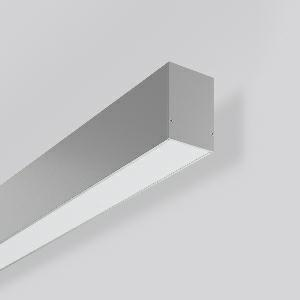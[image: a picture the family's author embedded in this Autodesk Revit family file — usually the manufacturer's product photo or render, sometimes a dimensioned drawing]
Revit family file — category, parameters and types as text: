
# Revit family: less_is_more_50_312607_0045_1_136a
name_source: partatom
category: Lighting Fixtures
units: mm (PartAtom-declared; Revit-internal decimal feet)

## family parameters
Cut with Voids When Loaded = No
Host = Face
Light Source = No
Part Type = Normal
Room Calculation Point = No
Round Connector Dimension = Use Diameter
Shared = No

## types (1)
- LESS IS MORE 50 (1 x LED Modul 840, 1500 lm, 4000)
    Apparent Load = 12 VA
    CIE Flux Codes = 48 80 96 100 100
    Color Rendering = 80
    Color Temperature = 4000
    Default Elevation = 1800 mm
    Description = Series: LESS IS MORE 50
Linear wall luminaires. Housing: extruded aluminium profile, powder-coated. End cap aluminium powder-coated. Diffuser made of non-yellowing plastic (PMMA), opal. Direct light emission. Suitable for Wall (surface). LED unit with integrated converter interchangeable and removable. Suitable for through-wiring. With sensors or as a safety luminaire on request. 
Colour: white aluminium (RAL 9006)
Length: 1127 mm
Width: 67 mm
Height: 75 mm
Lamp: LED
Socket: without socket
Colour temperature: 4000K
Colour rendering index (CRI): 80
System power: 12 W
Rated luminous flux: 1500 lm
Luminous efficiency: 125 lm/W
Control gear: Regulated power supply
Protection class: I
Type of protection: IP 20
    Height = 75 mm
    Lamp = 1 x LED Modul 840
    Lamp Light Flux = 1500 lm
    Lamp count = 1
    Length = 1127 mm
    Lifetime = 50000 h
    Luminous efficacy = 125 lm/W
    Manufacturer = RZB
    ModVariant = No
    Model = 312607.0045.1
    Mounting Place = Wall
    Mounting Type = Surface mounted
    Number of Poles = 1
    OnlyDefault = Yes
    Power Factor = 1
    Product Name = LESS IS MORE 50
    Product group = Surface mounted LED linear luminaires
    ProductGroupID = 2007
    Protection Class = Protection class I
    Protection Degree = IP 20
    RLX_Detail_Level = 1
    RLX_Emergency_Light_Flux = 0 lm
    RLX_Emergency_Type = 0
    RLX_Emergency_Type_DB = No
    RlxData = <blob elided: 40209 chars, md5=ca228e26>
    Socket = socket
    Standby Power = 0 W
    System Light Flux = 1500 lm
    System Power = 12 W
    Type Comments = Product without accessories
    Type Image = 312606.004.jpg
    URL = http://relux.com
    VarID = ---
    Voltage = 0 V
    Weight = 0.00 kg
    Width = 67 mm

## geometry (parser evidence)
native form markers: Blend x4, Sweep x13
no freeform markers — native parametric forms only
